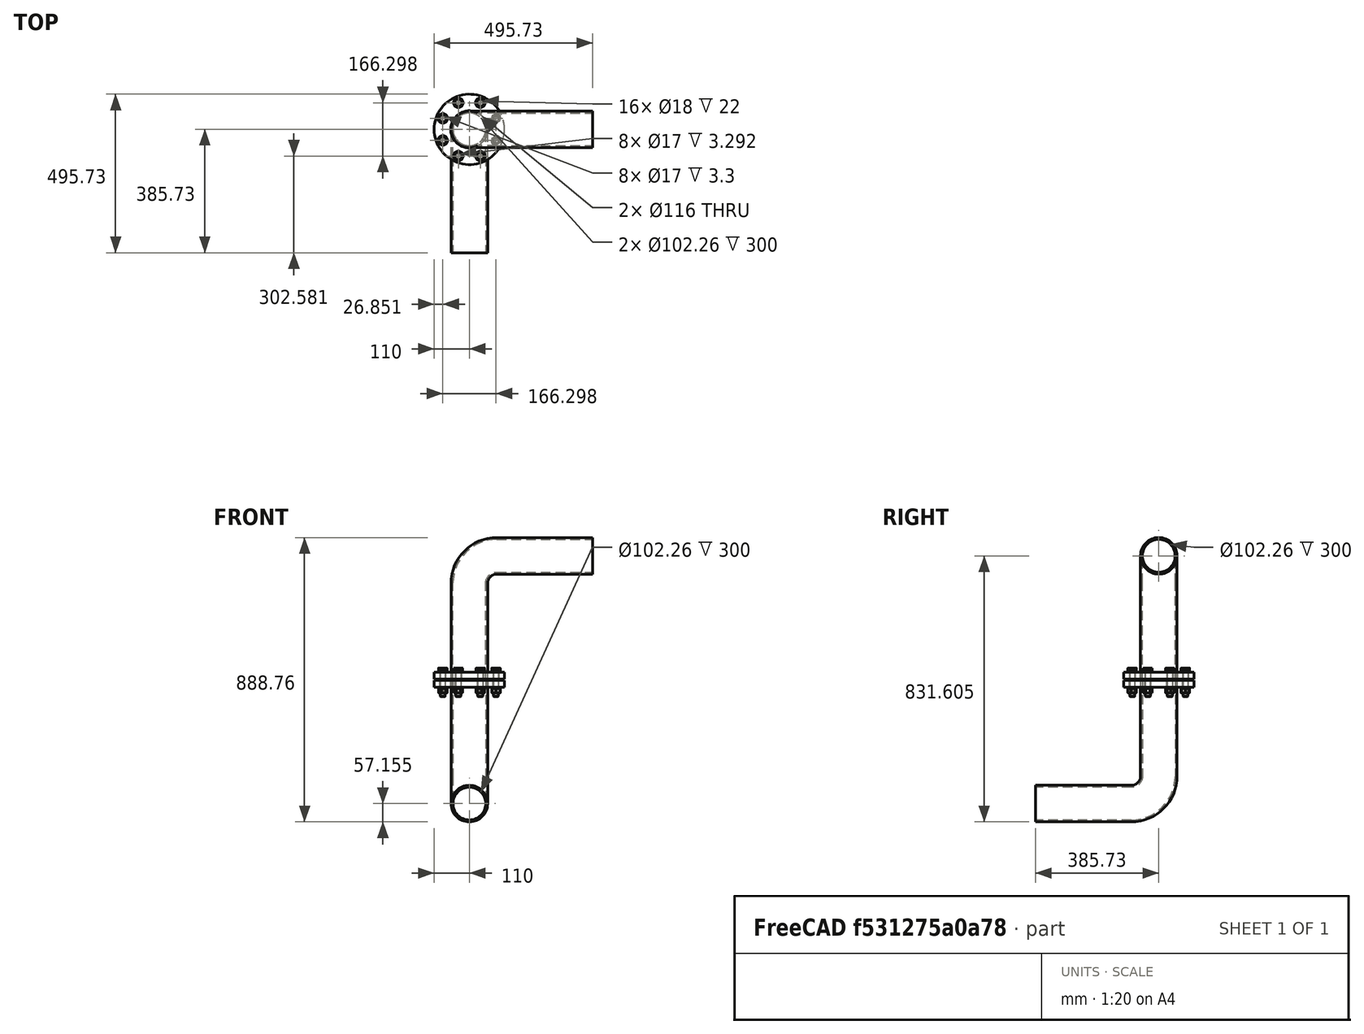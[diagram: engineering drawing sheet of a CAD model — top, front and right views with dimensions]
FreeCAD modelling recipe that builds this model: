
FCSTD DOCUMENT  (FreeCAD 0.17R13247 (Git))
Label: TUBULAÇÃO
License: All rights reserved
LicenseURL: http://en.wikipedia.org/wiki/All_rights_reserved
objects: Part::FeaturePython×16, Part::MultiFuse×3
note: 19 computed .brp shape members not serialized (recipe doc carries the construction recipe); baked Part::Feature solids carry a one-line shape summary decoded from their .brp

FEATURE [Part::FeaturePython] Flangia  # WARN: FeaturePython — macro-defined, semantics opaque (R4)
  D = 220
  FlangeType = SO
  PRating = DIN-PN16
  PSize = DN100
  PType = Flange
  d = 116
  df = 180
  f = 18
  n = 8
  t = 22
FEATURE [Part::FeaturePython] Tubo001  # WARN: FeaturePython — macro-defined, semantics opaque (R4)
  Height = 300
  ID = 102.26
  OD = 114.3
  PRating = SCH-STD
  PSize = DN100
  PType = Pipe
  Profile = 114.3 mmx6.02 mm
  thk = 6.02
FEATURE [Part::FeaturePython] Curva  # WARN: FeaturePython — macro-defined, semantics opaque (R4)
  BendAngle = 90
  BendRadius = 85.725
  ID = 102.26
  OD = 114.3
  PRating = SCH-STD
  PSize = DN100
  PType = Elbow
  Placement = pos=(0,0,385.725) rot=(-1,0,0;1.5708rad)
  Ports = (2) [(-1.00486e-14,85.725,0),(85.725,-1.00486e-14,0)]
  Profile = 114.3 mmx6.02 mm
  thk = 6.02
FEATURE [Part::FeaturePython] Tubo  # WARN: FeaturePython — macro-defined, semantics opaque (R4)
  Height = 300
  ID = 102.26
  OD = 114.3
  PRating = SCH-STD
  PSize = DN100
  PType = Pipe
  Placement = pos=(85.725,2e-12,385.725) rot=(0,1,0;1.5708rad)
  Profile = 114.3 mmx6.02 mm
  thk = 6.02
FEATURE [Part::MultiFuse] Fusion
  Shapes = -> [Flangia,Tubo001,Curva,Tubo]
FEATURE [Part::FeaturePython] Flangia001  # WARN: FeaturePython — macro-defined, semantics opaque (R4)
  D = 220
  FlangeType = SO
  PRating = DIN-PN16
  PSize = DN100
  PType = Flange
  d = 116
  df = 180
  f = 18
  n = 8
  t = 22
FEATURE [Part::FeaturePython] Curva001  # WARN: FeaturePython — macro-defined, semantics opaque (R4)
  BendAngle = 90
  BendRadius = 85.725
  ID = 102.26
  OD = 114.3
  PRating = SCH-STD
  PSize = DN100
  PType = Elbow
  Placement = pos=(0,0,385.725) rot=(-1,0,0;1.5708rad)
  Ports = (2) [(-1.00486e-14,85.725,0),(85.725,-1.00486e-14,0)]
  Profile = 114.3 mmx6.02 mm
  thk = 6.02
FEATURE [Part::FeaturePython] Tubo002  # WARN: FeaturePython — macro-defined, semantics opaque (R4)
  Height = 300
  ID = 102.26
  OD = 114.3
  PRating = SCH-STD
  PSize = DN100
  PType = Pipe
  Profile = 114.3 mmx6.02 mm
  thk = 6.02
FEATURE [Part::FeaturePython] Tubo003  # WARN: FeaturePython — macro-defined, semantics opaque (R4)
  Height = 300
  ID = 102.26
  OD = 114.3
  PRating = SCH-STD
  PSize = DN100
  PType = Pipe
  Placement = pos=(85.725,2e-12,385.725) rot=(0,1,0;1.5708rad)
  Profile = 114.3 mmx6.02 mm
  thk = 6.02
FEATURE [Part::MultiFuse] Fusion001
  Placement = pos=(0,0,-3) rot=(0.707107,-0.707107,0;3.14159rad)
  Shapes = -> [Flangia001,Tubo002,Curva001,Tubo003]
FEATURE [Part::FeaturePython] Washer  label="M16-Washer"  # Fasteners workbench fastener (typed FeaturePython)
  Placement = pos=(-34.4415,-83.1492,22) rot=(0,0,1;0rad)
  baseObject = -> Fusion [Edge30]
  diameter = 11
  invert = false
  matchOuter = false
  offset = 0
  type = 0
FEATURE [Part::FeaturePython] Washer001  label="M16-Washer001"  # Fasteners workbench fastener (typed FeaturePython)
  Placement = pos=(-34.4415,-83.1492,-25) rot=(-1,0,0;3.14159rad)
  baseObject = -> Fusion001 [Edge39]
  diameter = 11
  invert = false
  matchOuter = false
  offset = 0
  type = 0
FEATURE [Part::FeaturePython] Screw  label="M16x80-Screw"  # Fasteners workbench fastener (typed FeaturePython)
  Placement = pos=(-34.4415,-83.1492,25.3) rot=(0,0,1;0rad)
  baseObject = -> Washer [Edge1]
  diameter = 13
  invert = false
  length = 9
  matchOuter = false
  offset = 0
  thread = false
  type = 14
FEATURE [Part::FeaturePython] Nut  label="M16-Nut"  # Fasteners workbench fastener (typed FeaturePython)
  Placement = pos=(-34.4415,-83.1492,-28.3) rot=(-1,0,0;3.14159rad)
  baseObject = -> Washer001 [Edge1]
  diameter = 13
  invert = false
  matchOuter = false
  offset = 0
  thread = false
  type = 1
FEATURE [Part::FeaturePython] Array  # Draft array (typed FeaturePython)
  Angle = 360
  ArrayType = 1
  Axis = (0,0,1)
  Base = -> Washer
  Center = (0,0,0)
  Fuse = false
  IntervalAxis = (0,0,0)
  IntervalX = (1,0,0)
  IntervalY = (0,1,0)
  IntervalZ = (0,0,0)
  NumberPolar = 8
  NumberX = 2
  NumberY = 2
  NumberZ = 1
FEATURE [Part::FeaturePython] Array001  # Draft array (typed FeaturePython)
  Angle = 360
  ArrayType = 1
  Axis = (0,0,1)
  Base = -> Washer001
  Center = (0,0,0)
  Fuse = false
  IntervalAxis = (0,0,0)
  IntervalX = (1,0,0)
  IntervalY = (0,1,0)
  IntervalZ = (0,0,0)
  NumberPolar = 8
  NumberX = 2
  NumberY = 2
  NumberZ = 1
FEATURE [Part::FeaturePython] Array002  # Draft array (typed FeaturePython)
  Angle = 360
  ArrayType = 1
  Axis = (0,0,1)
  Base = -> Screw
  Center = (0,0,0)
  Fuse = false
  IntervalAxis = (0,0,0)
  IntervalX = (1,0,0)
  IntervalY = (0,1,0)
  IntervalZ = (0,0,0)
  NumberPolar = 8
  NumberX = 2
  NumberY = 2
  NumberZ = 1
FEATURE [Part::FeaturePython] Array003  # Draft array (typed FeaturePython)
  Angle = 360
  ArrayType = 1
  Axis = (0,0,1)
  Base = -> Nut
  Center = (0,0,0)
  Fuse = false
  IntervalAxis = (0,0,0)
  IntervalX = (1,0,0)
  IntervalY = (0,1,0)
  IntervalZ = (0,0,0)
  NumberPolar = 8
  NumberX = 2
  NumberY = 2
  NumberZ = 1
FEATURE [Part::MultiFuse] Fusion002
  Shapes = -> [Fusion,Fusion001,Array,Array001,Array002,Array003]
